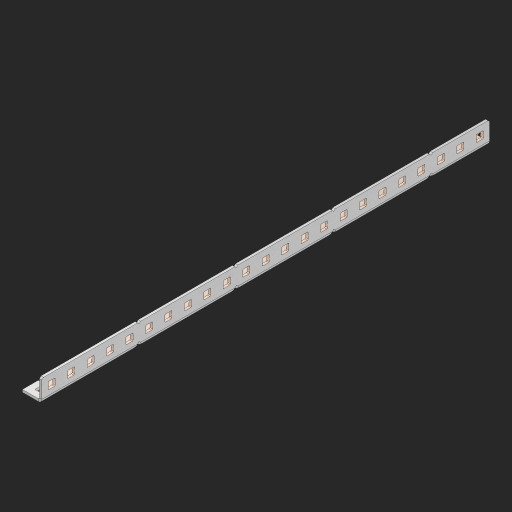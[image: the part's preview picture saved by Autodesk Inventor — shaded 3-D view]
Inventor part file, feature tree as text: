
AUTODESK INVENTOR PART (.ipt)
format: ipt  version: 2023 (Build 270158000, 158)  size: 1,069,056 bytes
history: native  units: in
note: dims shown in document units (in); Inventor stores cm internally (conversion verified against a paired STEP export)
features: other x217, extrude x67, sheet_metal_op x11, sketch x10, pattern_linear x2, mirror x1, chamfer x1
ambient origin geometry x8: Origin, YZ Plane, XZ Plane, XY Plane, X Axis, Y Axis, Z Axis, Center Point
bodies: Solid1 (feature_tree), Body (feature_tree)
feature tree (309):
  other  "Alu Half C 1x2x1x23"
  other  "Table"
  other  "Alu C 1x2x1x35"
  other  "Alu C 1x2x1x34"
  other  "Alu C 1x2x1x33"
  other  "Alu C 1x2x1x32"
  other  "Alu C 1x2x1x31"
  other  "Alu C 1x2x1x30"
  other  "Alu C 1x2x1x29"
  other  "Alu C 1x2x1x28"
  other  "Alu C 1x2x1x27"
  other  "Alu C 1x2x1x26"
  other  "Alu C 1x2x1x25"
  other  "Alu C 1x2x1x24"
  other  "Alu C 1x2x1x23"
  other  "Alu C 1x2x1x22"
  other  "Alu C 1x2x1x21"
  other  "Alu C 1x2x1x20"
  other  "Alu C 1x2x1x19"
  other  "Alu C 1x2x1x18"
  other  "Alu C 1x2x1x17"
  other  "Alu C 1x2x1x16"
  other  "Alu C 1x2x1x15"
  other  "Alu C 1x2x1x14"
  other  "Alu C 1x2x1x13"
  other  "Alu C 1x2x1x12"
  other  "Alu C 1x2x1x11"
  other  "Alu C 1x2x1x10"
  other  "Alu C 1x2x1x9"
  other  "Alu C 1x2x1x8"
  other  "Alu C 1x2x1x7"
  other  "Alu C 1x2x1x6"
  other  "Alu C 1x2x1x5"
  other  "Alu C 1x2x1x4"
  other  "Alu C 1x2x1x3"
  other  "Alu C 1x2x1x2"
  other  "Alu C 1x2x1x1"
  other  "Steel C 1x2x1x35"
  other  "Steel C 1x2x1x34"
  other  "Steel C 1x2x1x33"
  other  "Steel C 1x2x1x32"
  other  "Steel C 1x2x1x31"
  other  "Steel C 1x2x1x30"
  other  "Steel C 1x2x1x29"
  other  "Steel C 1x2x1x28"
  other  "Steel C 1x2x1x27"
  other  "Steel C 1x2x1x26"
  other  "Steel C 1x2x1x25"
  other  "Steel C 1x2x1x24"
  other  "Steel C 1x2x1x23"
  other  "Steel C 1x2x1x22"
  other  "Steel C 1x2x1x21"
  other  "Steel C 1x2x1x20"
  other  "Steel C 1x2x1x19"
  other  "Steel C 1x2x1x18"
  other  "Steel C 1x2x1x17"
  other  "Steel C 1x2x1x16"
  other  "Steel C 1x2x1x15"
  other  "Steel C 1x2x1x14"
  other  "Steel C 1x2x1x13"
  other  "Steel C 1x2x1x12"
  other  "Steel C 1x2x1x11"
  other  "Steel C 1x2x1x10"
  other  "Steel C 1x2x1x9"
  other  "Steel C 1x2x1x8"
  other  "Steel C 1x2x1x7"
  other  "Steel C 1x2x1x6"
  other  "Steel C 1x2x1x5"
  other  "Steel C 1x2x1x4"
  other  "Steel C 1x2x1x3"
  other  "Steel C 1x2x1x2"
  other  "Steel C 1x2x1x1"
  other  "Alu Half C 1x2x1x35"
  other  "Alu Half C 1x2x1x34"
  other  "Alu Half C 1x2x1x33"
  other  "Alu Half C 1x2x1x32"
  other  "Alu Half C 1x2x1x31"
  other  "Alu Half C 1x2x1x30"
  other  "Alu Half C 1x2x1x29"
  other  "Alu Half C 1x2x1x28"
  other  "Alu Half C 1x2x1x27"
  other  "Alu Half C 1x2x1x26"
  other  "Alu Half C 1x2x1x25"
  other  "Alu Half C 1x2x1x24"
  other  "Alu Half C 1x2x1x22"
  other  "Alu Half C 1x2x1x21"
  other  "Alu Half C 1x2x1x20"
  other  "Alu Half C 1x2x1x19"
  other  "Alu Half C 1x2x1x18"
  other  "Alu Half C 1x2x1x17"
  other  "Alu Half C 1x2x1x16"
  other  "Alu Half C 1x2x1x15"
  other  "Alu Half C 1x2x1x14"
  other  "Alu Half C 1x2x1x13"
  other  "Alu Half C 1x2x1x12"
  other  "Alu Half C 1x2x1x11"
  other  "Alu Half C 1x2x1x10"
  other  "Alu Half C 1x2x1x9"
  other  "Alu Half C 1x2x1x8"
  other  "Alu Half C 1x2x1x7"
  other  "Alu Half C 1x2x1x6"
  other  "Alu Half C 1x2x1x5"
  other  "Alu Half C 1x2x1x4"
  other  "Alu Half C 1x2x1x3"
  other  "Alu Half C 1x2x1x2"
  other  "Alu Half C 1x2x1x1"
  other  "Steel Half C 1x2x1x35"
  other  "Steel Half C 1x2x1x34"
  other  "Steel Half C 1x2x1x33"
  other  "Steel Half C 1x2x1x32"
  other  "Steel Half C 1x2x1x31"
  other  "Steel Half C 1x2x1x30"
  other  "Steel Half C 1x2x1x29"
  other  "Steel Half C 1x2x1x28"
  other  "Steel Half C 1x2x1x27"
  other  "Steel Half C 1x2x1x26"
  other  "Steel Half C 1x2x1x25"
  other  "Steel Half C 1x2x1x24"
  other  "Steel Half C 1x2x1x23"
  other  "Steel Half C 1x2x1x22"
  other  "Steel Half C 1x2x1x21"
  other  "Steel Half C 1x2x1x20"
  other  "Steel Half C 1x2x1x19"
  other  "Steel Half C 1x2x1x18"
  other  "Steel Half C 1x2x1x17"
  other  "Steel Half C 1x2x1x16"
  other  "Steel Half C 1x2x1x15"
  other  "Steel Half C 1x2x1x14"
  other  "Steel Half C 1x2x1x13"
  other  "Steel Half C 1x2x1x12"
  other  "Steel Half C 1x2x1x11"
  other  "Steel Half C 1x2x1x10"
  other  "Steel Half C 1x2x1x9"
  other  "Steel Half C 1x2x1x8"
  other  "Steel Half C 1x2x1x7"
  other  "Steel Half C 1x2x1x6"
  other  "Steel Half C 1x2x1x5"
  other  "Steel Half C 1x2x1x4"
  other  "Steel Half C 1x2x1x3"
  other  "Steel Half C 1x2x1x2"
  other  "Steel Half C 1x2x1x1"
  sheet_metal_op  "Flanges"
  other  "Flange Pattern Plane"
  other  "Flange Pattern Sketch"
  sheet_metal_op  "Flange Pattern"
  sheet_metal_op  "Body Pattern"
  pattern_linear  "Center Pattern"  Spacing1=0.0625in  [1 undecoded]
  other  "Arc Length"
  mirror  "Notch Mirror"
  pattern_linear  "Notch Pattern"  Spacing1=0.182in  [1 undecoded]
  chamfer  "End Chamfer"
  extrude  "Half Cut"  Depth=0.02in
  sketch  "Sketch1"  dims[d0=1.0in]
  other  "Plate1"
  sketch  "Sketch2"  dims[d1=11.5in]
  other  "Plate2"
  sheet_metal_op  "Bend1"
  sheet_metal_op  "Corner1"
  sketch  "Sketch3"  dims[d2=0.0625in]
  sketch  "Sketch7"  dims[d3=0.0625in]
  other  "Srf1"
  other  "Srf2"
  sketch  "Sketch8"  dims[d4=0.0312in]
  sketch  "Sketch9"  dims[d5=0.125in]
  other  "Srf91"
  sheet_metal_op  "Body Pattern Sketch"
  other  "Srf92"
  sketch  "Sketch13"  dims[d6=0.0625in]
  sketch  "Sketch14"  dims[d7=0.5in d8=90.0deg d9=0.0312in]
  sketch  "Sketch15"  dims[d10=0.25in]
  sketch  "Sketch16"  dims[d11=0.0625in d12=0.0625in d16=0.182in d17=0.02in d18=0.0625in d19=0.0in d20=0.25in d21=0.25in d38=9.0551in d40=0.5in d41=0.3937in d43=1.0in d46=0.172in d47=1.0in d48=0.0in d49=0.182in d50=0.02in d51=0.25in d52=0.25in d53=0.0625in d54=0.0in d55=0.172in d56=1.0in d57=0.0in d58=0.25in d60=9.0551in d62=0.5in d63=0.3937in d65=0.5in d85=0.1473in d86=0.1782in d88=0.04in d89=0.0625in d90=0.0in d91=0.04in d92=0.0491in d95=2.5in d96=0.04in d97=0.25in d98=45.0deg d99=0.25in d100=0.5in d101=0.0in d102=2.497in d106=0.182in d107=0.02in d108=0.5in d109=0.5in d110=0.0625in d111=0.0in d112=0.172in d113=0.5in d114=0.0in d117=0.5in d118=0.5in d119=0.5in]
  other  "Srf786"
  other  "Srf823"
  other  "Srf824"
  other  "Srf825"
  other  "Srf826"
  other  "Srf827"
  other  "Srf828"
  other  "Srf829"
  other  "Srf856"
  other  "Srf857"
  other  "Srf858"
  other  "Srf859"
  other  "Srf860"
  other  "Srf861"
  other  "Srf862"
  other  "Srf889"
  other  "Srf890"
  other  "Srf891"
  other  "Srf892"
  other  "Srf893"
  other  "Srf894"
  other  "Srf895"
  other  "Srf896"
  other  "Srf922"
  other  "Srf923"
  other  "Srf924"
  other  "Srf925"
  other  "Srf926"
  other  "Srf959"
  other  "Srf960"
  other  "Srf961"
  other  "Srf962"
  other  "Srf963"
  other  "Srf996"
  other  "Srf997"
  other  "Srf998"
  other  "Srf999"
  other  "Srf1000"
  other  "Srf1143"
  other  "Srf1144"
  other  "Srf1145"
  other  "Srf1146"
  other  "Srf1147"
  other  "Srf1148"
  other  "Srf1149"
  other  "Srf1150"
  other  "Srf1151"
  other  "Srf1199"
  other  "Srf1200"
  other  "Srf1201"
  other  "Srf1202"
  other  "Srf1203"
  other  "Srf1204"
  other  "Srf1205"
  other  "Srf1206"
  other  "Srf1207"
  other  "Srf1255"
  other  "Srf1256"
  other  "Srf1257"
  other  "Srf1258"
  other  "Srf1259"
  other  "Srf1260"
  other  "Srf1261"
  other  "Srf1262"
  other  "Srf1263"
  sheet_metal_op  "Flange Stamp"
  sheet_metal_op  "Flange Circle"
  sheet_metal_op  "Body Stamp"
  sheet_metal_op  "Body Circle"
  other  "Center Stamp"
  other  "Center Circle"
  sheet_metal_op  "Notch"
  extrude  "ExtrusionSrf2"  Depth=0.0625in
  extrude  "ExtrusionSrf92"  TaperAngle=0.0deg  [1 undecoded]
  extrude  "ExtrusionSrf823"  Depth=0.5in
  extrude  "ExtrusionSrf824"  Depth=0.5in
  extrude  "ExtrusionSrf825"  Depth=0.5in
  extrude  "ExtrusionSrf826"  Depth=0.5in
  extrude  "ExtrusionSrf827"  Depth=1.0in TaperAngle=0.0deg
  extrude  "ExtrusionSrf828"  Depth=0.182in
  extrude  "ExtrusionSrf829"  Depth=0.02in
  extrude  "ExtrusionSrf856"  Depth=0.5in
  extrude  "ExtrusionSrf857"  Depth=0.5in
  extrude  "ExtrusionSrf858"  Depth=0.0625in
  extrude  "ExtrusionSrf859"  TaperAngle=0.0deg  [1 undecoded]
  extrude  "ExtrusionSrf860"  Depth=0.5in
  extrude  "ExtrusionSrf861"  Depth=1.0in TaperAngle=0.0deg
  extrude  "ExtrusionSrf862"  Depth=0.5in
  extrude  "ExtrusionSrf889"  Depth=0.5in
  extrude  "ExtrusionSrf890"  Depth=0.5in
  extrude  "ExtrusionSrf891"  Depth=0.5in
  extrude  "ExtrusionSrf892"  Depth=0.5in
  extrude  "ExtrusionSrf893"  Depth=0.5in
  extrude  "ExtrusionSrf894"  Depth=0.0625in
  extrude  "ExtrusionSrf895"  TaperAngle=0.0deg  [1 undecoded]
  extrude  "ExtrusionSrf896"  Depth=0.5in
  extrude  "ExtrusionSrf922"  Depth=0.5in
  extrude  "ExtrusionSrf923"  Depth=0.5in
  extrude  "ExtrusionSrf924"  Depth=0.5in TaperAngle=45.0deg
  extrude  "ExtrusionSrf925"  Depth=0.5in
  extrude  "ExtrusionSrf926"  Depth=0.5in TaperAngle=0.0deg
  extrude  "ExtrusionSrf959"  Depth=0.5in
  extrude  "ExtrusionSrf960"  Depth=0.182in
  extrude  "ExtrusionSrf961"  Depth=0.02in
  extrude  "ExtrusionSrf962"  Depth=0.5in
  extrude  "ExtrusionSrf963"  Depth=0.5in
  extrude  "ExtrusionSrf996"  Depth=0.0625in
  extrude  "ExtrusionSrf997"  TaperAngle=0.0deg  [1 undecoded]
  extrude  "ExtrusionSrf998"  Depth=0.5in
  extrude  "ExtrusionSrf999"  Depth=0.5in TaperAngle=0.0deg
  extrude  "ExtrusionSrf1000"  Depth=0.5in
  extrude  "ExtrusionSrf1143"  Depth=0.5in
  extrude  "ExtrusionSrf1144"  Depth=0.5in
  extrude  "ExtrusionSrf1145"  [1 undecoded]
  extrude  "ExtrusionSrf1146"  [1 undecoded]
  extrude  "ExtrusionSrf1147"  [1 undecoded]
  extrude  "ExtrusionSrf1148"  [1 undecoded]
  extrude  "ExtrusionSrf1149"  [1 undecoded]
  extrude  "ExtrusionSrf1150"  [1 undecoded]
  extrude  "ExtrusionSrf1151"  [1 undecoded]
  extrude  "ExtrusionSrf1199"  [1 undecoded]
  extrude  "ExtrusionSrf1200"  [1 undecoded]
  extrude  "ExtrusionSrf1201"  [1 undecoded]
  extrude  "ExtrusionSrf1202"  [1 undecoded]
  extrude  "ExtrusionSrf1203"  [1 undecoded]
  extrude  "ExtrusionSrf1204"  [1 undecoded]
  extrude  "ExtrusionSrf1205"  [1 undecoded]
  extrude  "ExtrusionSrf1206"  [1 undecoded]
  extrude  "ExtrusionSrf1207"  [1 undecoded]
  extrude  "ExtrusionSrf1255"  [1 undecoded]
  extrude  "ExtrusionSrf1256"  [1 undecoded]
  extrude  "ExtrusionSrf1257"  [1 undecoded]
  extrude  "ExtrusionSrf1258"  [1 undecoded]
  extrude  "ExtrusionSrf1259"  [1 undecoded]
  extrude  "ExtrusionSrf1260"  [1 undecoded]
  extrude  "ExtrusionSrf1261"  [1 undecoded]
  extrude  "ExtrusionSrf1262"  [1 undecoded]
  extrude  "ExtrusionSrf1263"  [1 undecoded]
note: 31 required parameter values undecoded (feature->parameter linkage not recoverable at this tier; creation-order binding heuristic only, values carry confidence <= 0.55)
